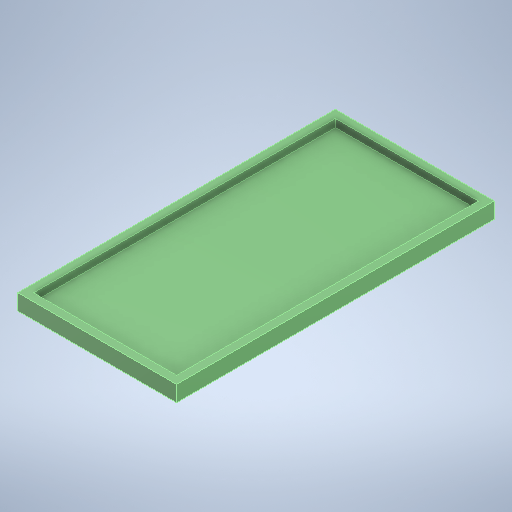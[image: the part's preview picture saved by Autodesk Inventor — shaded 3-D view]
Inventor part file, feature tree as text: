
AUTODESK INVENTOR PART (.ipt)
format: ipt  version: 2025 (Build 290162000, 162)  size: 245,760 bytes
history: native  units: in
note: dims shown in document units (in); Inventor stores cm internally (conversion verified against a paired STEP export)
features: extrude x2, sketch x1
ambient origin geometry x8: Origin, YZ Plane, XZ Plane, XY Plane, X Axis, Y Axis, Z Axis, Center Point
bodies: Solid1 (feature_tree)
feature tree (3):
  sketch  "Sketch1"  dims[d0=20.0in d1=10.0in d2=19.0in d3=9.0in d4=0.5in d5=0.0in d6=1.0in d7=0.0in]
  extrude  "Extrusion1"  Depth=10.0in
  extrude  "Extrusion2"  Depth=19.0in
